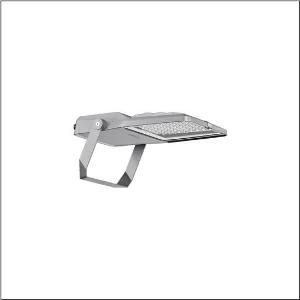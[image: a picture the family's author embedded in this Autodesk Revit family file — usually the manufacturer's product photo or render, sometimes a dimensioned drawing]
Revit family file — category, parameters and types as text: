
# Revit family: floodlight_fl_21_iq_mini___rs12_5xa7772c3b1a_483e
name_source: partatom
category: Lighting Fixtures
units: mm (PartAtom-declared; Revit-internal decimal feet)

## family parameters
Cut with Voids When Loaded = No
Host = Face
Light Source = No
Part Type = Normal
Room Calculation Point = No
Round Connector Dimension = Use Diameter
Shared = No

## types (1)
- --- (1 x LED, 10620 lm, 87.2 W, 3000K)
    Apparent Load = 87 VA
    CIE Flux Codes = 79 92 99 100 100
    Color Rendering = 80
    Color Temperature = 3000K
    Default Elevation = 1800 mm
    Description = Floodlight FL 21 iQ mini, floodlight, primary light control with lens, of PMMA, primary optical cover: protective disc, of toughened safety glass, transparent, light distribution: RS12, light emission: direct distribution, installation type: surface-mounted, LED, High Power LED, rated luminous flux: 10.620lm, luminous efficacy: 122lm/W, light colour: 830, colour temperature: 3000K, control: Street-Remote, Auto-Match, Temp-Guard, Night-Set, Smart-Wire, Desk-Remote (wireless, voltage-free reading and setting of iQ features in the workshop via application-optimized NFC function/RFID function), optimised constant luminous flux control (CLO 2.0), with terminal, 6-pole, mains connection: 220..240V, AC, 50/60Hz, start of lifetime: 87W, end of service life: 92W, reduction: 40W, luminaire housing, of diecast aluminium, powder-coated, Siteco® metallic grey (DB 702S), corrosivity category C5 mid according to DIN EN ISO 12944, sealing non-destructively replaceable, mounting bracket, of steel, galvanised, powder-coated, Siteco® metallic grey (DB 702S), protection rating (complete): IP66, insulation class (complete): insulation class II (safety insulation), certification: CE, ENEC, VDE, protection symbol: D, impact resistance: IK08, permissible operating ambient temperature: -40..+40°C, permissible operating ambient temperature for outdoor applications: -40..+50°C, standard: DIN EN 12944, LABS conformity tested according to VDMA 24364:2018-05, packaging unit: 1 piece

Light Distribution: RS12
    Height = 70 mm
    Lamp = 1 x LED
    Lamp Light Flux = 10620 lm
    Lamp Power = 87.2 W
    Lamp count = 1
    Length = 485 mm
    Luminous efficacy = 122 lm/W
    Manufacturer = Siteco
    ModVariant = No
    Model = 5XA7772C3B1A
    Number of Poles = 1
    OnlyDefault = Yes
    Power Factor = 1
    Product Name = Floodlight FL 21 iQ mini | RS12
    Product group = floodlight | pylon annexe
    ProductGroupID = 6200
    Protection Class = Protection class II
    Protection Degree = IP 66
    RLX_Detail_Level = 1
    RLX_Emergency_Light_Flux = 0 lm
    RLX_Emergency_Type = 0
    RLX_Emergency_Type_DB = No
    RlxData = <blob elided: 90941 chars, md5=22ba5295>
    Socket = socket
    Standby Power = 0 W
    System Light Flux = 10620 lm
    System Power = 87 W
    Type Comments = factory setting: luminous flux: 100 % | dim-lin: 254 | 456 mA
    Type Image = l_1006845.jpg
    URL = http://relux.com
    VarID = @adj_117767
    Voltage = 0 V
    Weight = 0.00 kg
    Width = 337 mm

## geometry (parser evidence)
native form markers: Blend x4, Sweep x14
no freeform markers — native parametric forms only
